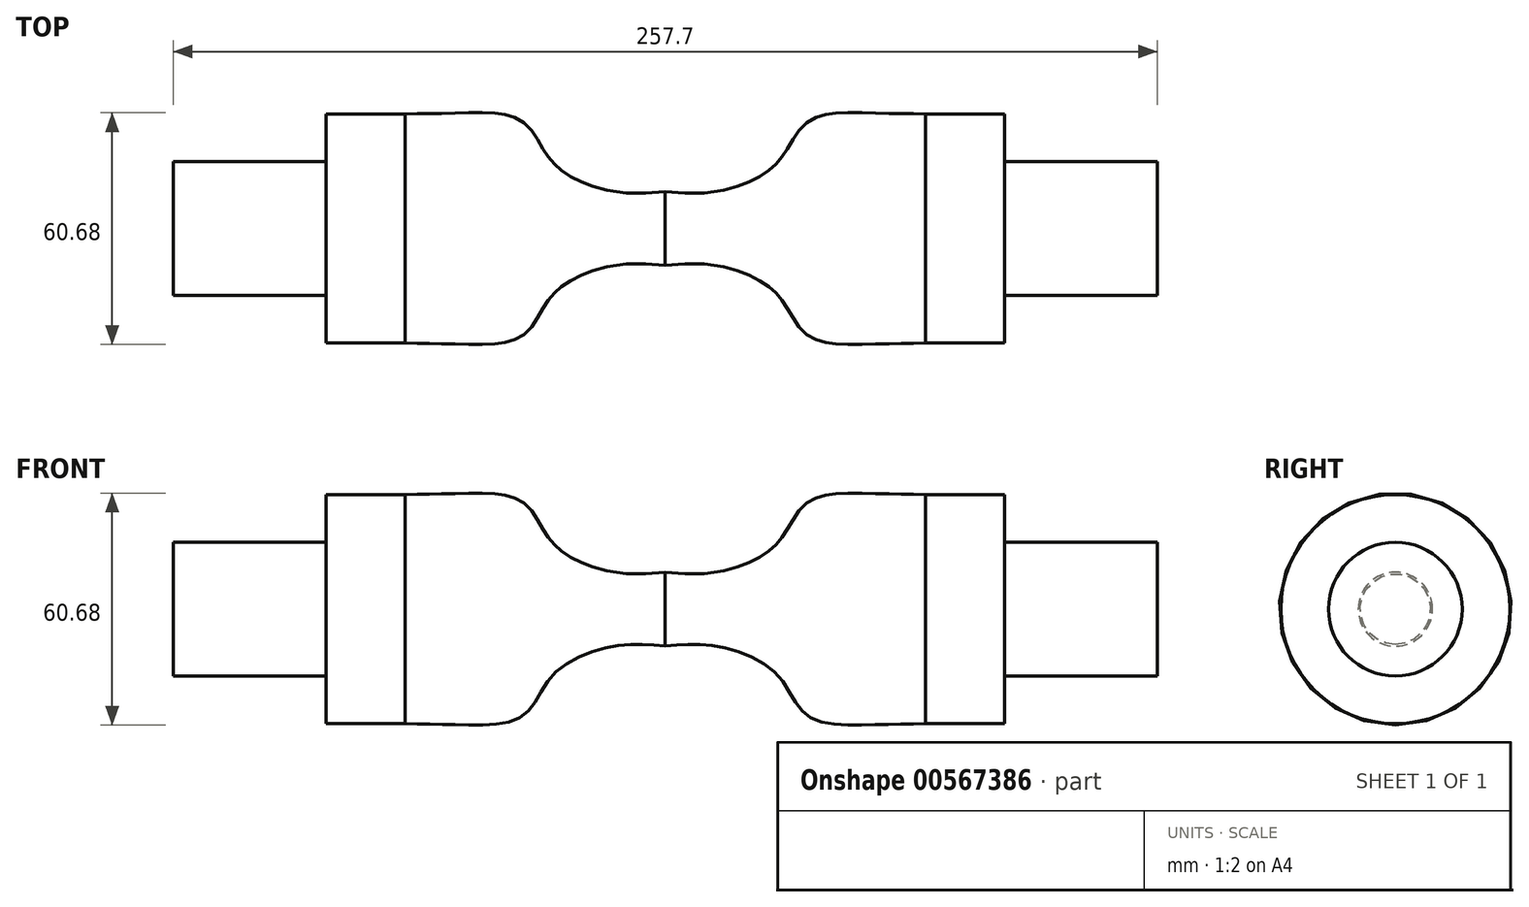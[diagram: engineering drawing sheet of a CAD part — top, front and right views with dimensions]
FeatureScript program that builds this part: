
annotation { "Feature Type Name" : "Feature", "Feature Type Description" : "" }
export const myFeature = defineFeature(function(context is Context, id is Id, definition is map)
    precondition{}
    {
        {
            var Q0;
            Q0=qCreatedBy(makeId("Front.planeOp"),FACE);
            var sketch = newSketch(context, id + "F0", { "sketchPlane" : qUnion([Q0])});
            skLineSegment(sketch, "E0", {"start": v(0, 0) * mm, "end": v(0, 9.7) * mm});
            skLineSegment(sketch, "E1", {"start": v(68.12, 30) * mm, "end": v(88.85, 30) * mm});
            skLineSegment(sketch, "E2", {"start": v(88.85, 30) * mm, "end": v(88.85, 17.5) * mm});
            skLineSegment(sketch, "E3", {"start": v(88.85, 17.5) * mm, "end": v(128.85, 17.5) * mm});
            skLineSegment(sketch, "E4", {"start": v(128.85, 17.5) * mm, "end": v(128.85, 0) * mm});
            skLineSegment(sketch, "E5", {"start": v(128.85, 0) * mm, "end": v(0, 0) * mm});
            skFitSpline(sketch, "E6", {"points": [v(0, 9.7) * mm, v(13.51, 9.7) * mm, v(29.35, 17.24) * mm, v(37.27, 27.96) * mm, v(52.65, 30.29) * mm, v(68.12, 30) * mm], "startDerivative": vector(67.9, -6.47) * mm, "endDerivative": vector(73.35, -1.25) * mm});
            skSolve(sketch);
        }
        {
            var Q0;
            Q0=makeQuery(id+"F0.imprint","IMPRINT",FACE,{"disambiguationData":[TD([[makeQuery(id+"F0.imprint","IMPRINT",EDGE,{"derivedFrom":sQuery(id+"F0.wireOp",EDGE,"E0")}),-1.0]])]});
            var Q1;
            Q1=sQuery(id+"F0.wireOp",EDGE,"E5");
            revolve(context, id + "F1", {"entities" : qUnion([Q0]), "axis" : qUnion([Q1]), "revolveType" : RevolveType.FULL});
        }
        {
            var Q0;
            Q0=makeQuery(id+"F1.opRevolve","SWEPT_BODY",BODY,{"disambiguationData":[OSD([sQuery(id+"F0.wireOp",EDGE,"E0"),sQuery(id+"F0.wireOp",EDGE,"E1"),sQuery(id+"F0.wireOp",EDGE,"E2"),sQuery(id+"F0.wireOp",EDGE,"E3"),sQuery(id+"F0.wireOp",EDGE,"E4"),sQuery(id+"F0.wireOp",EDGE,"E5"),sQuery(id+"F0.wireOp",EDGE,"E6")])]});
            var Q1;
            Q1=makeQuery(id+"F1.opRevolve","SWEPT_FACE",FACE,{"disambiguationData":[OSD([sQuery(id+"F0.wireOp",EDGE,"E0")])]});
            mirror(context, id + "F2", {"operationType" : NewBodyOperationType.ADD, "entities" : qUnion([Q0]), "mirrorPlane" : qUnion([Q1])});
        }
    });
